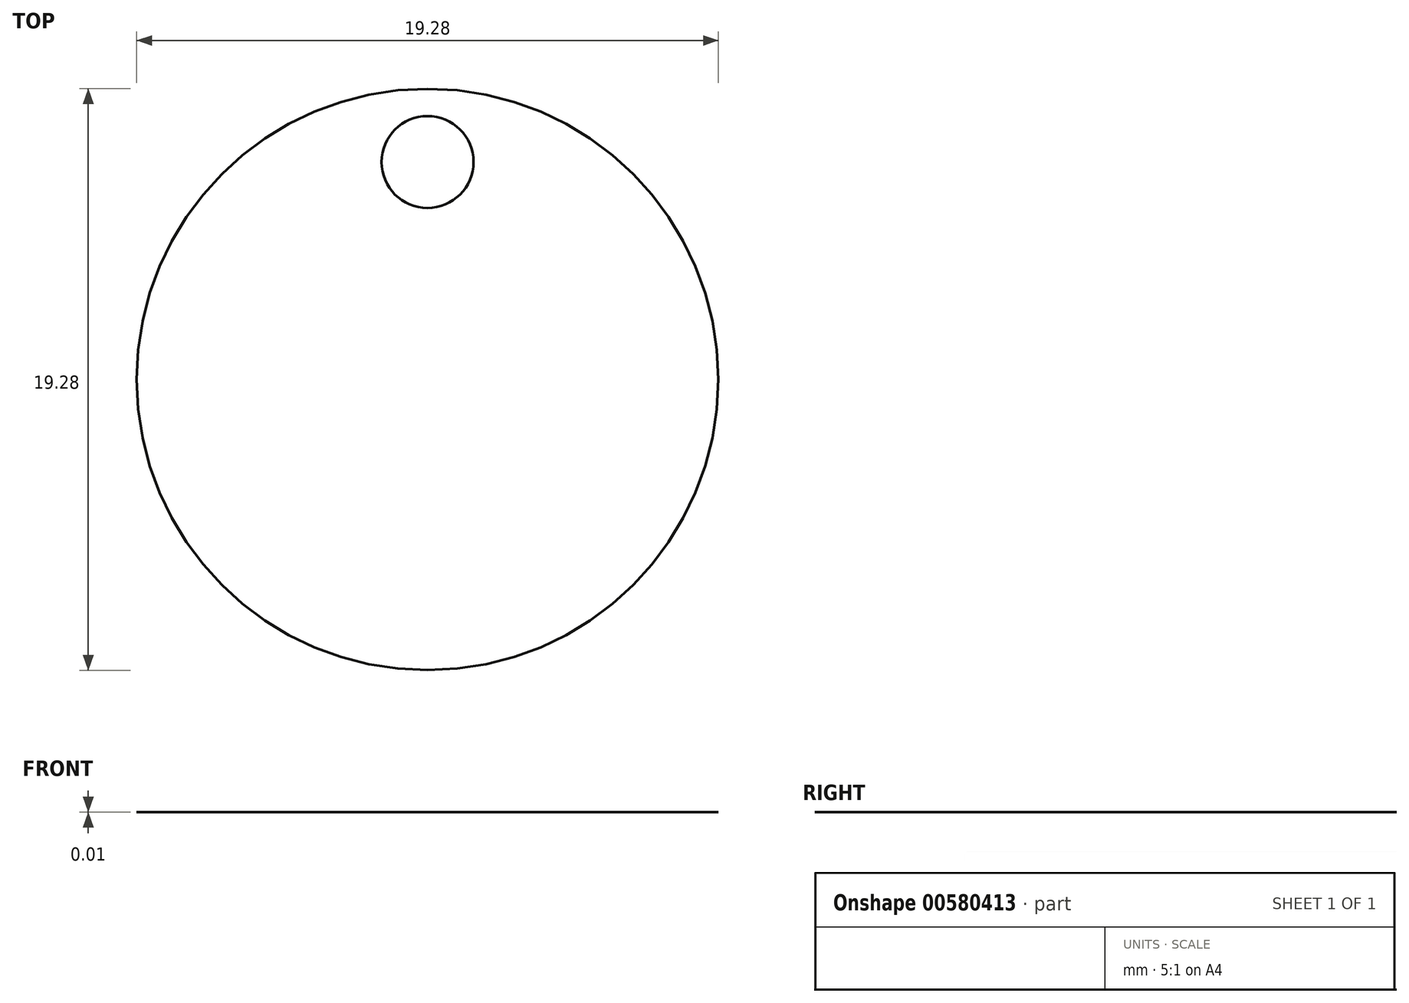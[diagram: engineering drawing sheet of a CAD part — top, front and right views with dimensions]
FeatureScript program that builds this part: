
annotation { "Feature Type Name" : "Feature", "Feature Type Description" : "" }
export const myFeature = defineFeature(function(context is Context, id is Id, definition is map)
    precondition{}
    {
        {
            var Q0;
            Q0=qCreatedBy(makeId("Top.planeOp"),FACE);
            var sketch = newSketch(context, id + "F0", { "sketchPlane" : qUnion([Q0])});
            skCircle(sketch, "E0", {"center": v(0, 0) * mm, "radius": 9.64 * mm});
            skSolve(sketch);
        }
        {
            var Q0;
            Q0=makeQuery(id+"F0.imprint","IMPRINT",FACE,{"disambiguationData":[TD([[makeQuery(id+"F0.imprint","IMPRINT",EDGE,{"derivedFrom":sQuery(id+"F0.wireOp",EDGE,"E0")}),1.0]])]});
            extrude(context, id + "F1", {"entities" : qUnion([Q0]), "depth" : 1 / 101.6 * mm, "offsetDistance" : 25.4 * mm});
        }
        {
            var Q0;
            Q0=makeQuery(id+"F1.opExtrude","CAP_FACE",FACE,{"disambiguationData":[OSD([sQuery(id+"F0.wireOp",EDGE,"E0")])],"isStart":false});
            var sketch = newSketch(context, id + "F2", { "sketchPlane" : qUnion([Q0])});
            skCircle(sketch, "E1", {"center": v(0.74, 5.81) * mm, "radius": 1.58 * mm});
            skPoint(sketch, "E1.first.point", {"position": v(0, 7.21) * mm});
            skPoint(sketch, "E1.second.point", {"position": v(2.33, 5.81) * mm});
            skPoint(sketch, "E1.third.point", {"position": v(0, 4.42) * mm});
            skSolve(sketch);
        }
        {
            var Q0;
            Q0=sQuery(id+"F2.wireOp",VERTEX,"E1.first.point");
            var Q1;
            Q1=makeQuery(id+"F1.opExtrude","SWEPT_BODY",BODY,{"disambiguationData":[OSD([sQuery(id+"F0.wireOp",EDGE,"E0")])]});
            hole(context, id + "F3", {"style" : HoleStyle.SIMPLE, "endStyle" : HoleEndStyle.THROUGH, "holeDiameter" : 3.05 * mm, "isTappedThrough" : true, "tappedDepth" : 12.7 * mm, "tapClearance" : 3, "locations" : qUnion([Q0]), "scope" : qUnion([Q1])});
        }
        {
            var Q0;
            Q0=makeQuery(id+"F1.opExtrude","CAP_FACE",FACE,{"disambiguationData":[OSD([sQuery(id+"F0.wireOp",EDGE,"E0")])],"isStart":false});
            fillet(context, id + "F4", {"entities" : qUnion([Q0]), "radius" : 5.08 * mm, "tangentPropagation" : true, "allowEdgeOverflow" : false});
        }
    });
